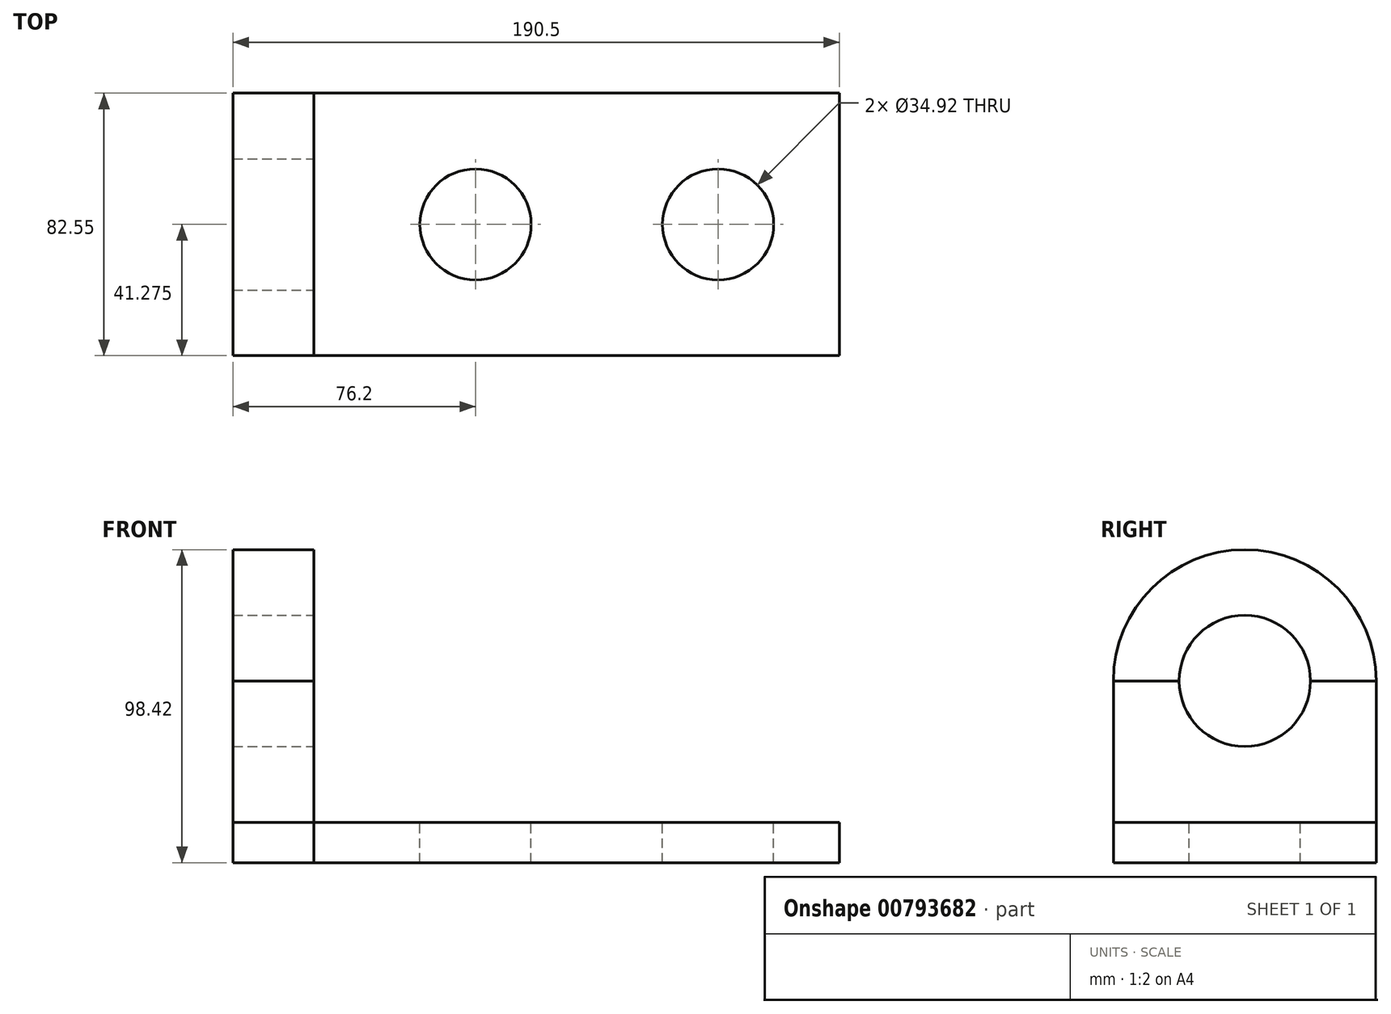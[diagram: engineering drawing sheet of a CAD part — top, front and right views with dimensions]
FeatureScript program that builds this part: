
annotation { "Feature Type Name" : "Feature", "Feature Type Description" : "" }
export const myFeature = defineFeature(function(context is Context, id is Id, definition is map)
    precondition{}
    {
        {
            var Q0;
            Q0=qCreatedBy(makeId("Front.planeOp"),FACE);
            var sketch = newSketch(context, id + "F0", { "sketchPlane" : qUnion([Q0])});
            skLineSegment(sketch, "E0", {"start": v(0, 0) * mm, "end": v(190.5, 0) * mm});
            skLineSegment(sketch, "E1", {"start": v(190.5, 0) * mm, "end": v(190.5, 12.7) * mm});
            skLineSegment(sketch, "E2", {"start": v(190.5, 12.7) * mm, "end": v(0, 12.7) * mm});
            skLineSegment(sketch, "E3", {"start": v(0, 12.7) * mm, "end": v(0, 0) * mm});
            skSolve(sketch);
        }
        {
            var Q0;
            Q0=makeQuery(id+"F0.imprint","IMPRINT",FACE,{"disambiguationData":[TD([[makeQuery(id+"F0.imprint","IMPRINT",EDGE,{"derivedFrom":sQuery(id+"F0.wireOp",EDGE,"E0")}),1.0]])]});
            extrude(context, id + "F1", {"entities" : qUnion([Q0]), "depth" : 82.55 * mm, "offsetDistance" : 25.4 * mm});
        }
        {
            var Q0;
            Q0=qCreatedBy(makeId("Right.planeOp"),FACE);
            var sketch = newSketch(context, id + "F2", { "sketchPlane" : qUnion([Q0])});
            skLineSegment(sketch, "E4", {"start": v(0, 0) * mm, "end": v(0, 101.6) * mm});
            skLineSegment(sketch, "E5", {"start": v(0, 101.6) * mm, "end": v(-82.55, 101.6) * mm});
            skLineSegment(sketch, "E6", {"start": v(-82.55, 101.6) * mm, "end": v(-82.55, 0) * mm});
            skLineSegment(sketch, "E7", {"start": v(0, 0) * mm, "end": v(-82.55, 0) * mm});
            skSolve(sketch);
        }
        {
            var Q0;
            Q0=makeQuery(id+"F2.imprint","IMPRINT",FACE,{"disambiguationData":[TD([[makeQuery(id+"F2.imprint","IMPRINT",EDGE,{"derivedFrom":sQuery(id+"F2.wireOp",EDGE,"E4")}),1.0]])]});
            extrude(context, id + "F3", {"entities" : qUnion([Q0]), "depth" : 25.4 * mm, "offsetDistance" : 25.4 * mm});
        }
        {
            var Q0;
            Q0=makeQuery(id+"F3.opExtrude","CAP_FACE",FACE,{"disambiguationData":[OSD([sQuery(id+"F2.wireOp",EDGE,"E4"),sQuery(id+"F2.wireOp",EDGE,"E5"),sQuery(id+"F2.wireOp",EDGE,"E6"),sQuery(id+"F2.wireOp",EDGE,"E7")])],"isStart":false});
            var sketch = newSketch(context, id + "F4", { "sketchPlane" : qUnion([Q0])});
            skLineSegment(sketch, "E8", {"start": v(-82.55, 0) * mm, "end": v(-82.55, 57.15) * mm});
            skLineSegment(sketch, "E9", {"start": v(-82.55, 57.15) * mm, "end": v(0, 57.15) * mm});
            skLineSegment(sketch, "E10", {"start": v(0, 57.15) * mm, "end": v(0, 0) * mm});
            skLineSegment(sketch, "E11", {"start": v(0, 0) * mm, "end": v(-82.55, 0) * mm});
            skSolve(sketch);
        }
        {
            var Q0;
            {var subQ0=sQuery(id+"F4.wireOp",EDGE,"E9");Q0=makeQuery(id+"F4.imprint","IMPRINT",FACE,{"disambiguationData":[TD([[makeQuery(id+"F4.imprint","IMPRINT",EDGE,{"derivedFrom":subQ0}),1.0]])]});}
            extrude(context, id + "F5", {"entities" : qUnion([Q0]), "operationType" : NewBodyOperationType.REMOVE, "oppositeDirection" : true, "depth" : 25.4 * mm, "offsetDistance" : 25.4 * mm});
        }
        {
            var Q0;
            Q0=makeQuery(id+"F3.opExtrude","CAP_FACE",FACE,{"disambiguationData":[OSD([sQuery(id+"F2.wireOp",EDGE,"E4"),sQuery(id+"F2.wireOp",EDGE,"E5"),sQuery(id+"F2.wireOp",EDGE,"E6"),sQuery(id+"F2.wireOp",EDGE,"E7")])],"isStart":false});
            var sketch = newSketch(context, id + "F6", { "sketchPlane" : qUnion([Q0])});
            skArc(sketch, "E12", {"start": v(0, 57.15) * mm, "mid": v(-41.28, 98.43) * mm, "end": v(-82.55, 57.15) * mm});
            skSolve(sketch);
        }
        {
            var Q0;
            Q0 = qSketchRegion(id + "F6", true);
            var Q1;
            Q1=makeQuery(id+"F6.imprint","IMPRINT",FACE,{"disambiguationData":[TD([[makeQuery(id+"F6.imprint","IMPRINT",EDGE,{"derivedFrom":sQuery(id+"F6.wireOp",EDGE,"E12")}),1.0]])]});
            extrude(context, id + "F7", {"entities" : qUnion([Q0, Q1]), "oppositeDirection" : true, "depth" : 25.4 * mm, "offsetDistance" : 25.4 * mm});
        }
        {
            var Q0;
            Q0=makeQuery(id+"F3.opExtrude","CAP_FACE",FACE,{"disambiguationData":[OSD([sQuery(id+"F2.wireOp",EDGE,"E4"),sQuery(id+"F2.wireOp",EDGE,"E5"),sQuery(id+"F2.wireOp",EDGE,"E6"),sQuery(id+"F2.wireOp",EDGE,"E7")])],"isStart":false});
            var sketch = newSketch(context, id + "F8", { "sketchPlane" : qUnion([Q0])});
            skCircle(sketch, "E13", {"center": v(-41.28, 57.15) * mm, "radius": 41.28 * mm});
            skCircle(sketch, "E14", {"center": v(-41.28, 57.15) * mm, "radius": 20.64 * mm});
            skSolve(sketch);
        }
        {
            var Q0;
            {var subQ0=sQuery(id+"F8.wireOp",EDGE,"E14");var subQ1=makeQuery(id+"F5.boolean.opBoolean","COPY",EDGE,{"derivedFrom":makeQuery(id+"F5.opExtrude","CAP_EDGE",EDGE,{"disambiguationData":[OSD([sQuery(id+"F4.wireOp",EDGE,"E9")])],"isStart":true})});var subQ2=makeQuery(id+"F8.imprint","INTERSECT",VERTEX,{"disambiguationData":[OD(0.0)],"derivedFrom":[subQ1,subQ0]});Q0=makeQuery(id+"F8.imprint","IMPRINT",FACE,{"disambiguationData":[TD([[makeQuery(id+"F8.imprint","IMPRINT",EDGE,{"disambiguationData":[TD([[subQ2,1.0]])],"derivedFrom":subQ0}),1.0]])]});}
            extrude(context, id + "F9", {"entities" : qUnion([Q0]), "operationType" : NewBodyOperationType.REMOVE, "oppositeDirection" : true, "depth" : 25.4 * mm, "offsetDistance" : 25.4 * mm});
        }
        {
            var Q0;
            {var subQ0=sQuery(id+"F8.wireOp",EDGE,"E14");var subQ1=makeQuery(id+"F5.boolean.opBoolean","COPY",EDGE,{"derivedFrom":makeQuery(id+"F5.opExtrude","CAP_EDGE",EDGE,{"disambiguationData":[OSD([sQuery(id+"F4.wireOp",EDGE,"E9")])],"isStart":true})});var subQ2=makeQuery(id+"F8.imprint","INTERSECT",VERTEX,{"disambiguationData":[OD(0.0)],"derivedFrom":[subQ1,subQ0]});Q0=makeQuery(id+"F8.imprint","IMPRINT",FACE,{"disambiguationData":[TD([[makeQuery(id+"F8.imprint","IMPRINT",EDGE,{"disambiguationData":[TD([[subQ2,-1.0]])],"derivedFrom":subQ0}),1.0]])]});}
            extrude(context, id + "F10", {"entities" : qUnion([Q0]), "operationType" : NewBodyOperationType.REMOVE, "oppositeDirection" : true, "depth" : 25.4 * mm, "offsetDistance" : 25.4 * mm});
        }
        {
            var Q0;
            Q0=makeQuery(id+"F1.opExtrude","SWEPT_FACE",FACE,{"disambiguationData":[OSD([sQuery(id+"F0.wireOp",EDGE,"E2")])]});
            var sketch = newSketch(context, id + "F11", { "sketchPlane" : qUnion([Q0])});
            skLineSegment(sketch, "E15", {"start": v(190.5, -41.28) * mm, "end": v(152.4, -41.28) * mm, "construction": true});
            skCircle(sketch, "E16", {"center": v(152.4, -41.28) * mm, "radius": 17.46 * mm});
            skLineSegment(sketch, "E17", {"start": v(152.4, -41.28) * mm, "end": v(76.2, -41.28) * mm, "construction": true});
            skCircle(sketch, "E18", {"center": v(76.2, -41.28) * mm, "radius": 17.46 * mm});
            skSolve(sketch);
        }
        {
            var Q0;
            Q0 = qSketchRegion(id + "F11", true);
            extrude(context, id + "F12", {"entities" : qUnion([Q0]), "operationType" : NewBodyOperationType.REMOVE, "oppositeDirection" : true, "depth" : 25.4 * mm, "offsetDistance" : 25.4 * mm});
        }
    });
